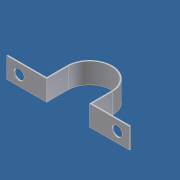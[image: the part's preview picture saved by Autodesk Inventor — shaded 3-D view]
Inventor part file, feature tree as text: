
AUTODESK INVENTOR PART (.ipt)
format: ipt  version: unknown  size: 201,728 bytes
history: native  units: mm
features: sketch x2, extrude x1, hole x1, mirror x1
ambient origin geometry x8: Origin, YZ Plane, XZ Plane, XY Plane, X Axis, Y Axis, Z Axis, Center Point
bodies: Solido1 (feature_tree)
feature tree (5):
  extrude  "Estrusione1"  Depth=10.0mm TaperAngle=0.0deg
  hole  "Foro2"  [1 undecoded]
  mirror  "Specchio2"
  sketch  "Schizzo1"
  sketch  "Schizzo3"
note: 1 required parameter value undecoded (feature->parameter linkage not recoverable at this tier; creation-order binding heuristic only, values carry confidence <= 0.55)
